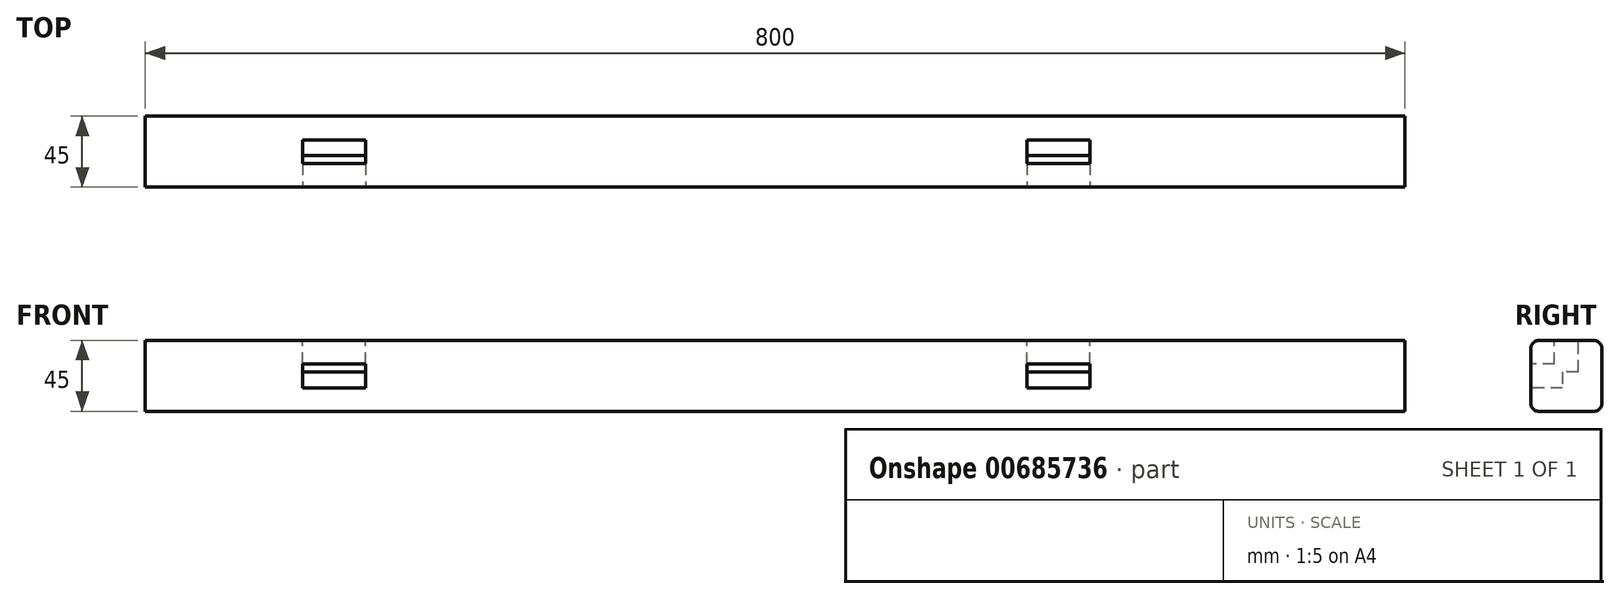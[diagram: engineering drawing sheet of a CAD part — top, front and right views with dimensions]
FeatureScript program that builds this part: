
annotation { "Feature Type Name" : "Feature", "Feature Type Description" : "" }
export const myFeature = defineFeature(function(context is Context, id is Id, definition is map)
    precondition{}
    {
        {
            var Q0;
            Q0=qCreatedBy(makeId("Right.planeOp"),FACE);
            var sketch = newSketch(context, id + "F0", { "sketchPlane" : qUnion([Q0])});
            skLineSegment(sketch, "E0.bottom", {"start": v(22.5, 22.5) * mm, "end": v(-22.5, 22.5) * mm});
            skLineSegment(sketch, "E0.top", {"start": v(22.5, -22.5) * mm, "end": v(-22.5, -22.5) * mm});
            skLineSegment(sketch, "E0.left", {"start": v(22.5, 22.5) * mm, "end": v(22.5, -22.5) * mm});
            skLineSegment(sketch, "E0.right", {"start": v(-22.5, 22.5) * mm, "end": v(-22.5, -22.5) * mm});
            skPoint(sketch, "E0.middle", {"position": v(0, 0) * mm});
            skSolve(sketch);
        }
        {
            var Q0;
            Q0=qSketchRegion(id+"F0",true);
            extrude(context, id + "F1", {"entities" : qUnion([Q0]), "endBound" : BoundingType.SYMMETRIC, "depth" : 800 * mm, "offsetDistance" : 25 * mm});
        }
        {
            var Q0;
            Q0=makeQuery(id+"F1.opExtrude","SWEPT_EDGE",EDGE,{"disambiguationData":[OSD([sQuery(id+"F0.wireOp",EDGE,"E0.bottom"),sQuery(id+"F0.wireOp",EDGE,"E0.right")])]});
            var Q1;
            Q1=makeQuery(id+"F1.opExtrude","SWEPT_EDGE",EDGE,{"disambiguationData":[OSD([sQuery(id+"F0.wireOp",EDGE,"E0.bottom"),sQuery(id+"F0.wireOp",EDGE,"E0.left")])]});
            var Q2;
            Q2=makeQuery(id+"F1.opExtrude","SWEPT_EDGE",EDGE,{"disambiguationData":[OSD([sQuery(id+"F0.wireOp",EDGE,"E0.top"),sQuery(id+"F0.wireOp",EDGE,"E0.right")])]});
            var Q3;
            Q3=makeQuery(id+"F1.opExtrude","SWEPT_EDGE",EDGE,{"disambiguationData":[OSD([sQuery(id+"F0.wireOp",EDGE,"E0.top"),sQuery(id+"F0.wireOp",EDGE,"E0.left")])]});
            fillet(context, id + "F2", {"entities" : qUnion([Q0, Q1, Q2, Q3]), "radius" : 5 * mm, "tangentPropagation" : true, "allowEdgeOverflow" : false});
        }
        {
            var Q0;
            Q0=makeQuery(id+"F1.opExtrude","SWEPT_FACE",FACE,{"disambiguationData":[OSD([sQuery(id+"F0.wireOp",EDGE,"E0.bottom")])]});
            var sketch = newSketch(context, id + "F3", { "sketchPlane" : qUnion([Q0])});
            skLineSegment(sketch, "E1.bottom", {"start": v(-260, 7.5) * mm, "end": v(-300, 7.5) * mm});
            skLineSegment(sketch, "E1.top", {"start": v(-260, -7.5) * mm, "end": v(-300, -7.5) * mm});
            skLineSegment(sketch, "E1.left", {"start": v(-260, 7.5) * mm, "end": v(-260, -7.5) * mm});
            skLineSegment(sketch, "E1.right", {"start": v(-300, 7.5) * mm, "end": v(-300, -7.5) * mm});
            skPoint(sketch, "E1.middle", {"position": v(-280, 0) * mm});
            skSolve(sketch);
        }
        {
            var Q0;
            Q0=qSketchRegion(id+"F3",true);
            extrude(context, id + "F4", {"entities" : qUnion([Q0]), "operationType" : NewBodyOperationType.REMOVE, "oppositeDirection" : true, "depth" : 20 * mm, "offsetDistance" : 25 * mm});
        }
        {
            var Q0;
            Q0=makeQuery(id+"F1.opExtrude","SWEPT_FACE",FACE,{"disambiguationData":[OSD([sQuery(id+"F0.wireOp",EDGE,"E0.right")])]});
            var sketch = newSketch(context, id + "F5", { "sketchPlane" : qUnion([Q0])});
            skLineSegment(sketch, "E2.bottom", {"start": v(-260, 7.5) * mm, "end": v(-300, 7.5) * mm});
            skLineSegment(sketch, "E2.top", {"start": v(-260, -7.5) * mm, "end": v(-300, -7.5) * mm});
            skLineSegment(sketch, "E2.left", {"start": v(-260, 7.5) * mm, "end": v(-260, -7.5) * mm});
            skLineSegment(sketch, "E2.right", {"start": v(-300, 7.5) * mm, "end": v(-300, -7.5) * mm});
            skPoint(sketch, "E2.middle", {"position": v(-280, 0) * mm});
            skSolve(sketch);
        }
        {
            var Q0;
            Q0=qSketchRegion(id+"F5",true);
            extrude(context, id + "F6", {"entities" : qUnion([Q0]), "operationType" : NewBodyOperationType.REMOVE, "oppositeDirection" : true, "depth" : 20 * mm, "offsetDistance" : 25 * mm});
        }
        {
            var Q0;
            Q0=makeQuery(id+"F1.opExtrude","SWEPT_FACE",FACE,{"disambiguationData":[OSD([sQuery(id+"F0.wireOp",EDGE,"E0.bottom")])]});
            var sketch = newSketch(context, id + "F7", { "sketchPlane" : qUnion([Q0])});
            skLineSegment(sketch, "E3.bottom", {"start": v(160, 7.5) * mm, "end": v(200, 7.5) * mm});
            skLineSegment(sketch, "E3.top", {"start": v(160, -7.5) * mm, "end": v(200, -7.5) * mm});
            skLineSegment(sketch, "E3.left", {"start": v(160, 7.5) * mm, "end": v(160, -7.5) * mm});
            skLineSegment(sketch, "E3.right", {"start": v(200, 7.5) * mm, "end": v(200, -7.5) * mm});
            skPoint(sketch, "E3.middle", {"position": v(180, 0) * mm});
            skSolve(sketch);
        }
        {
            var Q0;
            Q0=makeQuery(id+"F7.imprint","IMPRINT",FACE,{"disambiguationData":[TD([[makeQuery(id+"F7.imprint","IMPRINT",EDGE,{"derivedFrom":sQuery(id+"F7.wireOp",EDGE,"E3.bottom")}),-1.0]])]});
            extrude(context, id + "F8", {"entities" : qUnion([Q0]), "operationType" : NewBodyOperationType.REMOVE, "oppositeDirection" : true, "depth" : 20 * mm, "offsetDistance" : 25 * mm});
        }
        {
            var Q0;
            Q0=makeQuery(id+"F1.opExtrude","SWEPT_FACE",FACE,{"disambiguationData":[OSD([sQuery(id+"F0.wireOp",EDGE,"E0.right")])]});
            var sketch = newSketch(context, id + "F9", { "sketchPlane" : qUnion([Q0])});
            skLineSegment(sketch, "E4.bottom", {"start": v(200, 7.5) * mm, "end": v(160, 7.5) * mm});
            skLineSegment(sketch, "E4.top", {"start": v(200, -7.5) * mm, "end": v(160, -7.5) * mm});
            skLineSegment(sketch, "E4.left", {"start": v(200, 7.5) * mm, "end": v(200, -7.5) * mm});
            skLineSegment(sketch, "E4.right", {"start": v(160, 7.5) * mm, "end": v(160, -7.5) * mm});
            skPoint(sketch, "E4.middle", {"position": v(180, 0) * mm});
            skSolve(sketch);
        }
        {
            var Q0;
            Q0=qSketchRegion(id+"F9",true);
            extrude(context, id + "F10", {"entities" : qUnion([Q0]), "operationType" : NewBodyOperationType.REMOVE, "oppositeDirection" : true, "depth" : 20 * mm, "offsetDistance" : 25 * mm});
        }
    });
